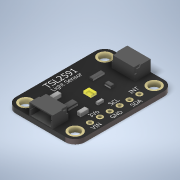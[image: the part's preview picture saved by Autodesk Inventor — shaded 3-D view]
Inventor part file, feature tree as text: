
AUTODESK INVENTOR PART (.ipt)
format: ipt  version: 2020 (Build 240168000, 168)  size: 1,448,960 bytes
history: native  units: mm
features: extrude x22, sketch x17, chamfer x12, fillet x2, hole x1
ambient origin geometry x8: Origin, YZ Plane, XZ Plane, XY Plane, X Axis, Y Axis, Z Axis, Center Point
bodies: Solide1 (feature_tree)
feature tree (54):
  extrude  "Extrusion1"  Depth=25.4mm
  hole  "Perçage1"  [1 undecoded]
  fillet  "Congé1"  Radius=1.2mm
  sketch  "Esquisse3"
  extrude  "Extrusion2"  Depth=2.54mm
  extrude  "Extrusion3"  Depth=2.54mm
  extrude  "Extrusion4"  Depth=0.8mm
  extrude  "Extrusion5"  Depth=2.54mm
  extrude  "Extrusion6"  Depth=60.0mm
  extrude  "Extrusion7"  Depth=1.5mm
  extrude  "Extrusion8"  Depth=3.54mm
  extrude  "Extrusion9"  Depth=60.0mm
  sketch  "Esquisse11"
  extrude  "Extrusion10"  Depth=1.2mm TaperAngle=0.0deg
  extrude  "Extrusion11"  Depth=0.01mm TaperAngle=0.0deg
  extrude  "Extrusion12"  Depth=0.01mm TaperAngle=0.0deg
  chamfer  "Chanfrein1"  Distance=3.0mm
  chamfer  "Chanfrein2"  Distance=4.1mm
  chamfer  "Chanfrein3"  Distance=6.0mm
  chamfer  "Chanfrein4"  Distance=3.0mm
  sketch  "Esquisse13"
  extrude  "Extrusion13"  Depth=1.5mm
  extrude  "Extrusion14"  Depth=0.5mm
  extrude  "Extrusion15"  Depth=1.0mm
  chamfer  "Chanfrein5"  Distance=1.0mm
  chamfer  "Chanfrein6"  Distance=0.3mm
  chamfer  "Chanfrein7"  Distance=0.3mm
  chamfer  "Chanfrein8"  Distance=0.3mm
  sketch  "Esquisse15"
  extrude  "Extrusion16"  Depth=1.5mm
  extrude  "Extrusion17"  Depth=0.5mm
  extrude  "Extrusion18"  Depth=0.3mm TaperAngle=0.0deg
  extrude  "Extrusion19"  Depth=0.1mm
  chamfer  "Chanfrein9"  Distance=0.1mm
  chamfer  "Chanfrein10"  Distance=3.0mm
  chamfer  "Chanfrein11"  Distance=0.15mm
  chamfer  "Chanfrein12"  Distance=0.4mm
  fillet  "Congé2"  Radius=0.4mm
  extrude  "Extrusion20"  Depth=1.5mm
  extrude  "Extrusion21"  Depth=0.2mm
  extrude  "Extrusion22"  Depth=0.2mm
  sketch  "Esquisse1"
  sketch  "Esquisse2"
  sketch  "Esquisse4"
  sketch  "Esquisse5"
  sketch  "Esquisse6"
  sketch  "Esquisse8"
  sketch  "Esquisse9"
  sketch  "Esquisse10"
  sketch  "Esquisse12"
  sketch  "Esquisse14"
  sketch  "Esquisse16"
  sketch  "Esquisse17"
  sketch  "Esquisse18"
note: 1 required parameter value undecoded (feature->parameter linkage not recoverable at this tier; creation-order binding heuristic only, values carry confidence <= 0.55)
